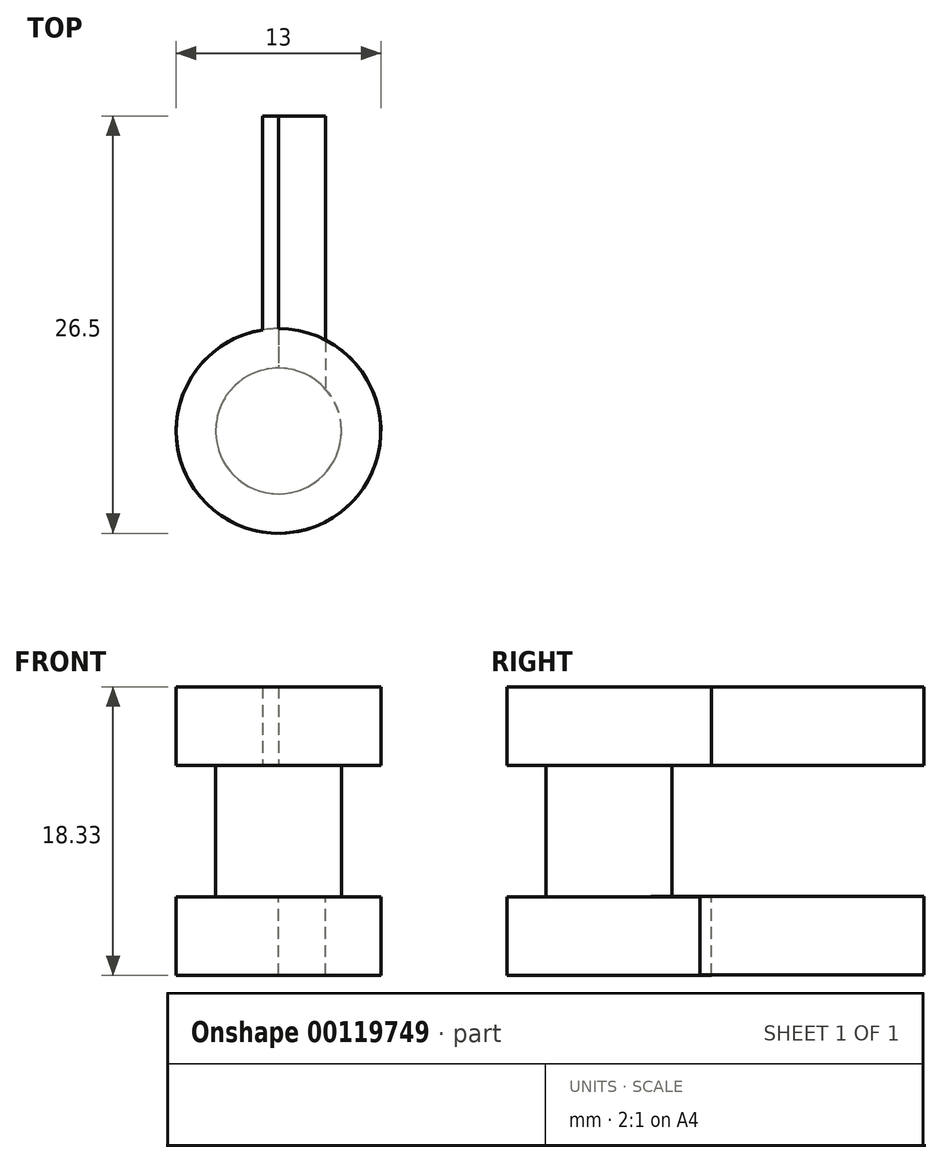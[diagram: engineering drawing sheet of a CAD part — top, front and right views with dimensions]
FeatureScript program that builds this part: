
annotation { "Feature Type Name" : "Feature", "Feature Type Description" : "" }
export const myFeature = defineFeature(function(context is Context, id is Id, definition is map)
    precondition{}
    {
        {
            var Q0;
            Q0=qCreatedBy(makeId("Top.planeOp"),FACE);
            var sketch = newSketch(context, id + "F0", { "sketchPlane" : qUnion([Q0])});
            skCircle(sketch, "E0", {"center": v(0, 0) * mm, "radius": 4 * mm});
            skSolve(sketch);
        }
        {
            var Q0;
            Q0 = qSketchRegion(id + "F0", true);
            extrude(context, id + "F1", {"entities" : qUnion([Q0]), "oppositeDirection" : true, "depth" : 8.33 * mm});
        }
        {
            var Q0;
            Q0=makeQuery(id+"F1.opExtrude","CAP_FACE",FACE,{"disambiguationData":[OSD([sQuery(id+"F0.wireOp",EDGE,"E0")])],"isStart":false});
            var sketch = newSketch(context, id + "F2", { "sketchPlane" : qUnion([Q0])});
            skCircle(sketch, "E1", {"center": v(0, 0) * mm, "radius": 6.5 * mm});
            skSolve(sketch);
        }
        {
            var Q0;
            Q0 = qSketchRegion(id + "F2", true);
            extrude(context, id + "F3", {"entities" : qUnion([Q0]), "operationType" : NewBodyOperationType.ADD, "depth" : 5 * mm});
        }
        {
            var Q0;
            Q0=makeQuery(id+"F1.opExtrude","CAP_FACE",FACE,{"disambiguationData":[OSD([sQuery(id+"F0.wireOp",EDGE,"E0")])],"isStart":true});
            var sketch = newSketch(context, id + "F4", { "sketchPlane" : qUnion([Q0])});
            skCircle(sketch, "E2", {"center": v(0, 0) * mm, "radius": 6.5 * mm});
            skSolve(sketch);
        }
        {
            var Q0;
            Q0 = qSketchRegion(id + "F4", true);
            extrude(context, id + "F5", {"entities" : qUnion([Q0]), "operationType" : NewBodyOperationType.ADD, "depth" : 5 * mm});
        }
        {
            var Q0;
            Q0=qCreatedBy(makeId("Right.planeOp"),FACE);
            var sketch = newSketch(context, id + "F6", { "sketchPlane" : qUnion([Q0])});
            skLineSegment(sketch, "E3", {"start": v(0, -13.3) * mm, "end": v(20, -13.3) * mm});
            skLineSegment(sketch, "E4", {"start": v(20, -13.3) * mm, "end": v(20, -8.32) * mm});
            skLineSegment(sketch, "E5", {"start": v(20, -8.32) * mm, "end": v(0, -8.32) * mm});
            skLineSegment(sketch, "E6", {"start": v(0, -8.32) * mm, "end": v(0, -13.3) * mm});
            skSolve(sketch);
        }
        {
            var Q0;
            Q0 = qSketchRegion(id + "F6", true);
            extrude(context, id + "F7", {"entities" : qUnion([Q0]), "operationType" : NewBodyOperationType.ADD, "depth" : 3 * mm});
        }
        {
            var Q0;
            Q0=qCreatedBy(makeId("Right.planeOp"),FACE);
            var sketch = newSketch(context, id + "F8", { "sketchPlane" : qUnion([Q0])});
            skLineSegment(sketch, "E7.bottom", {"start": v(0, 5) * mm, "end": v(20, 5) * mm});
            skLineSegment(sketch, "E7.top", {"start": v(0, 0) * mm, "end": v(20, 0) * mm});
            skLineSegment(sketch, "E7.left", {"start": v(0, 5) * mm, "end": v(0, 0) * mm});
            skLineSegment(sketch, "E7.right", {"start": v(20, 5) * mm, "end": v(20, 0) * mm});
            skSolve(sketch);
        }
        {
            var Q0;
            Q0=makeQuery(id+"F8.imprint","IMPRINT",FACE,{"disambiguationData":[TD([[makeQuery(id+"F8.imprint","IMPRINT",EDGE,{"derivedFrom":sQuery(id+"F8.wireOp",EDGE,"E7.bottom")}),-1.0]])]});
            extrude(context, id + "F9", {"entities" : qUnion([Q0]), "operationType" : NewBodyOperationType.ADD, "oppositeDirection" : true, "depth" : 1 * mm});
        }
    });
